# Revit family: Tyco_FireDtctnAlmCtrlIndctEquip_Zettler-AddressableHeatDetector
name_source: partatom
category: Fire Alarm Devices
revit_build: Autodesk Revit MEP 2013 (Build: 20120221_2030(x64)
units: mm (PartAtom-declared; Revit-internal decimal feet)

## types (2) — shared parameters
AlarmCurrent = 3.3mA
AssetType = Moveable
Brand = Zettler
Category = Ee_40_15_75
Color = White
Default Elevation = 1200 mm
Detector Color = Plastic Material White
DetectorType = Heat Detector
DurationUnit = Year
Features = Addressable Heat Sensor
HasProtectiveEarth = No
IPCode = IP44
IfcExportAs = IfcSensorType
IfcExportType = HEATSENSOR
IfcTypeObject = IfcBuildingElementProxy
Manufacturer = Tyco Fire Protection Products
ManufacturerName = Tyco Fire Protection Products
ManufacturerURL = www.zettlerfire.com
Material = Flame Retardant-FR3010 ‘BAYBLEND'
NBSDescription = Fire detection and alarm control and indicating equipment (CIE)
NBSReference = 90-75-30/380
NominalDiameter = 108 mm
NominalHeight = 42 mm
NominalLength = 108 mm
NominalVoltage = 40 V DC
NominalWidth = 108 mm
OperationTemperatureRange = -25 °C to +70 °C
PhaseAngle = 0.00°
ProductInformation = http://www.zettlerfire.com
QuiescentCurrent = 335μA
RelativeHumidity = 95%(non-condensing)
StorageTemperature = -40 °C to +80 °C
URL = http://www.zettlerfire.com
Uniclass2 = Ee_40_15_75
UsageCurrent = 335μA
Version = 1
Voltage = 20 – 40 VDC
WarrantyDurationLabor = 1.5 years
WarrantyDurationParts = 1.5 years
WarrantyDurationUnit = Year
Weight = (Excluding Base) 81g
zero-valued in all types: NumberOfPoles

## per-type parameters (varying)
| type | BIMObjectName | Description | DeviceBases | Name | ProductCodes | ProductSpecification | ShortCircuitIsolators | Type Comments |
| 850H | Tyco_FireDtctnAlmCtrlIndctEquip_Zettler-AddressableHeatDetector-850H | Zettler-Addressable Heat Detector with built in line isolator | 4B-C_Continuity Detector Base | 850H-Addressable Heat Detector | 516.850.053 | 850H Heat Detector with built in-line isolator | Yes | Only 4B-C_Continuity Detector Base can be used with 850H Detector |
| 830H | Tyco_FireDtctnAlmCtrlIndctEquip_Zettler-AddressableHeatDetector-830H | Zettler-Addressable Heat Detector without built in- line isolator | 4B_Detector Base/4B-I_Isolator Detector Base | 830H-Addressable Heat Detector | 516.830.053 | 830H Heat Detector without built in- line isolator | No | Only 4B_Detector or 4B-I_Isolator Detector Bases can be used with 830H Detector |

note: column(s) folded — value = type name in every type: Model, ModelNumber

## geometry (parser evidence)
native form markers: Sweep x4
no freeform markers — native parametric forms only
